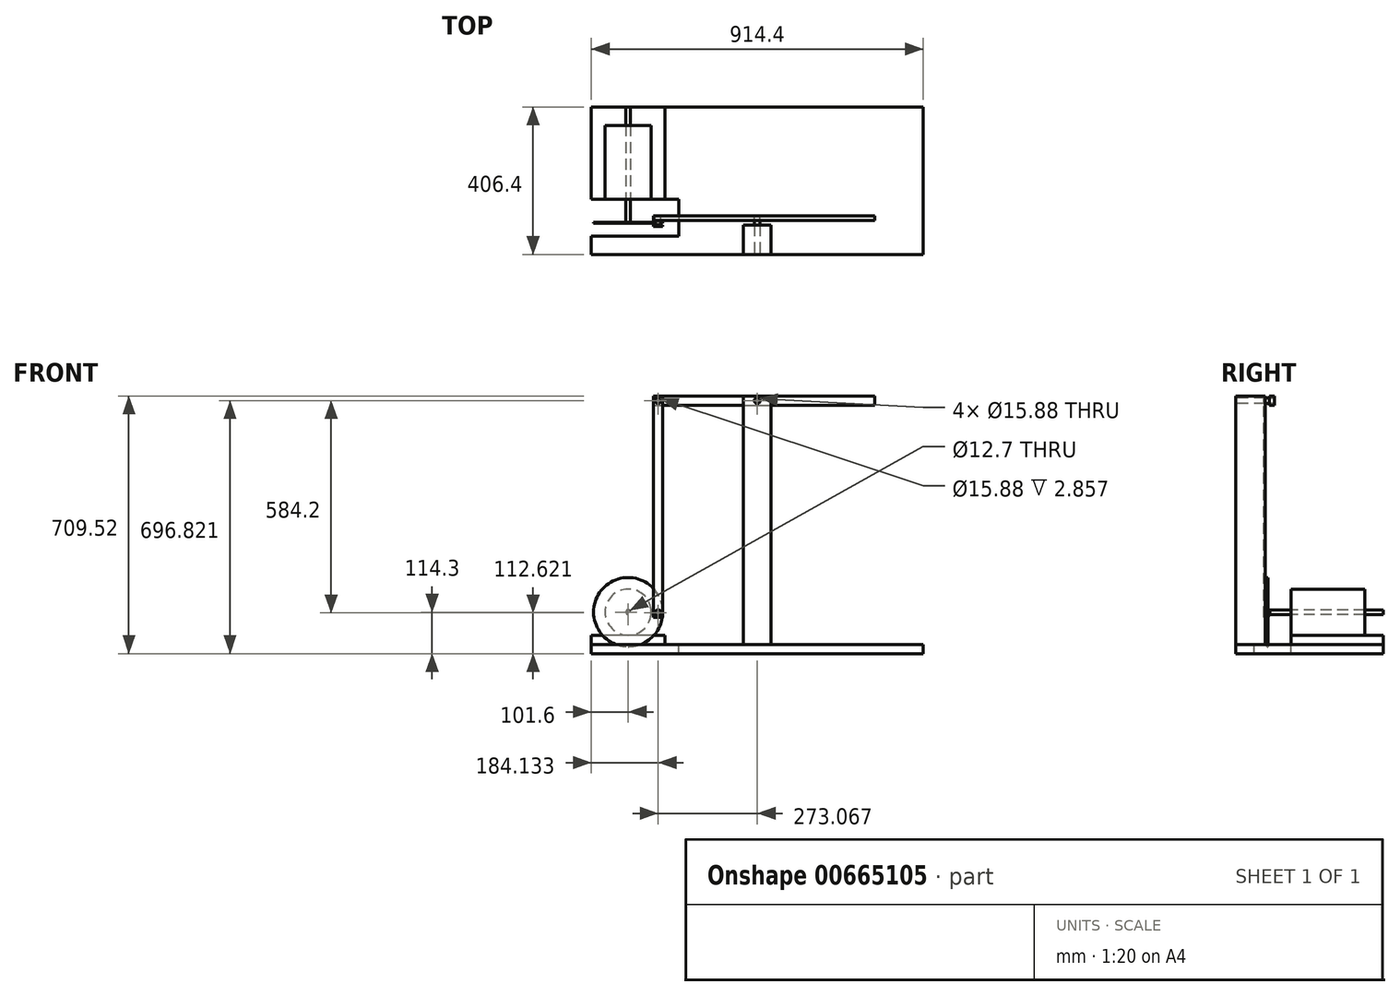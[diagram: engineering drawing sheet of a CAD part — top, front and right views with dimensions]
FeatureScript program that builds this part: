
annotation { "Feature Type Name" : "Feature", "Feature Type Description" : "" }
export const myFeature = defineFeature(function(context is Context, id is Id, definition is map)
    precondition{}
    {
        {
            var Q0;
            Q0=qCreatedBy(makeId("Top.planeOp"),FACE);
            var sketch = newSketch(context, id + "F0", { "sketchPlane" : qUnion([Q0])});
            skLineSegment(sketch, "E0.bottom", {"start": v(0, 0) * mm, "end": v(-203.2, 0) * mm});
            skLineSegment(sketch, "E0.top", {"start": v(0, -254) * mm, "end": v(-203.2, -254) * mm});
            skLineSegment(sketch, "E0.left", {"start": v(0, 0) * mm, "end": v(0, -254) * mm});
            skLineSegment(sketch, "E0.right", {"start": v(-203.2, 0) * mm, "end": v(-203.2, -254) * mm});
            skSolve(sketch);
        }
        {
            var Q0;
            Q0=makeQuery(id+"F0.imprint","IMPRINT",FACE,{"disambiguationData":[TD([[makeQuery(id+"F0.imprint","IMPRINT",EDGE,{"derivedFrom":sQuery(id+"F0.wireOp",EDGE,"E0.bottom")}),1.0]])]});
            extrude(context, id + "F1", {"entities" : qUnion([Q0]), "depth" : 25.4 * mm, "offsetDistance" : 25.4 * mm});
        }
        {
            var Q0;
            Q0=makeQuery(id+"F1.opExtrude","SWEPT_FACE",FACE,{"disambiguationData":[OSD([sQuery(id+"F0.wireOp",EDGE,"E0.top")])]});
            var sketch = newSketch(context, id + "F2", { "sketchPlane" : qUnion([Q0])});
            skLineSegment(sketch, "E1", {"start": v(-101.6, 25.4) * mm, "end": v(-101.6, 88.9) * mm, "construction": true});
            skCircle(sketch, "E2", {"center": v(-101.6, 88.9) * mm, "radius": 63.5 * mm});
            skCircle(sketch, "E3", {"center": v(-101.6, 88.9) * mm, "radius": 6.35 * mm});
            skSolve(sketch);
        }
        {
            var Q0;
            Q0 = qSketchRegion(id + "F2", true);
            extrude(context, id + "F3", {"entities" : qUnion([Q0]), "oppositeDirection" : true, "depth" : 203.2 * mm, "offsetDistance" : 25.4 * mm});
        }
        {
            var Q0;
            Q0=makeQuery(id+"F2.imprint","IMPRINT",FACE,{"disambiguationData":[TD([[makeQuery(id+"F2.imprint","IMPRINT",EDGE,{"derivedFrom":sQuery(id+"F2.wireOp",EDGE,"E3")}),1.0]])]});
            extrude(context, id + "F4", {"entities" : qUnion([Q0]), "depth" : 63.5 * mm, "offsetDistance" : 25.4 * mm, "hasSecondDirection" : true, "secondDirectionOppositeDirection" : true, "secondDirectionDepth" : 254 * mm});
        }
        {
            var Q0;
            Q0=makeQuery(id+"F4.opExtrude","CAP_FACE",FACE,{"disambiguationData":[OSD([sQuery(id+"F2.wireOp",EDGE,"E3")])],"isStart":false});
            var sketch = newSketch(context, id + "F5", { "sketchPlane" : qUnion([Q0])});
            skCircle(sketch, "E4.0", {"center": v(-101.6, 88.9) * mm, "radius": 6.35 * mm});
            skCircle(sketch, "E5", {"center": v(-101.6, 88.9) * mm, "radius": 95.25 * mm});
            skCircle(sketch, "E6", {"center": v(-101.6, 88.9) * mm, "radius": 82.55 * mm});
            skPoint(sketch, "E7", {"position": v(-19.07, 87.22) * mm});
            skCircle(sketch, "E8", {"center": v(-19.07, 87.22) * mm, "radius": 7.94 * mm});
            skSolve(sketch);
        }
        {
            var Q0;
            Q0=makeQuery(id+"F5.imprint","IMPRINT",FACE,{"disambiguationData":[TD([[makeQuery(id+"F5.imprint","IMPRINT",EDGE,{"derivedFrom":sQuery(id+"F5.wireOp",EDGE,"E5")}),1.0]])]});
            var Q1;
            Q1=makeQuery(id+"F5.imprint","IMPRINT",FACE,{"disambiguationData":[TD([[makeQuery(id+"F5.imprint","IMPRINT",EDGE,{"derivedFrom":sQuery(id+"F5.wireOp",EDGE,"E4.0")}),-1.0]])]});
            var Q2;
            Q2=makeQuery(id+"F5.imprint","IMPRINT",FACE,{"disambiguationData":[TD([[makeQuery(id+"F5.imprint","IMPRINT",EDGE,{"derivedFrom":sQuery(id+"F5.wireOp",EDGE,"E4.0")}),1.0]])]});
            extrude(context, id + "F6", {"entities" : qUnion([Q0, Q1, Q2]), "operationType" : NewBodyOperationType.ADD, "depth" : 3.17 * mm, "offsetDistance" : 25.4 * mm});
        }
        {
            var Q0;
            Q0=makeQuery(id+"F6.opExtrude","CAP_FACE",FACE,{"disambiguationData":[OSD([sQuery(id+"F5.wireOp",EDGE,"E5"),sQuery(id+"F5.wireOp",EDGE,"E8")])],"isStart":false});
            var sketch = newSketch(context, id + "F7", { "sketchPlane" : qUnion([Q0])});
            skCircle(sketch, "E9.0", {"center": v(-19.07, 87.22) * mm, "radius": 7.94 * mm});
            skSolve(sketch);
        }
        {
            var Q0;
            Q0=makeQuery(id+"F7.imprint","IMPRINT",FACE,{"disambiguationData":[TD([[makeQuery(id+"F7.imprint","IMPRINT",EDGE,{"derivedFrom":sQuery(id+"F7.wireOp",EDGE,"E9.0")}),1.0]])]});
            extrude(context, id + "F8", {"entities" : qUnion([Q0]), "operationType" : NewBodyOperationType.ADD, "endBound" : BoundingType.SYMMETRIC, "depth" : 15.88 * mm, "offsetDistance" : 25.4 * mm});
        }
        {
            var Q0;
            Q0=makeQuery(id+"F8.opExtrude","CAP_FACE",FACE,{"disambiguationData":[OSD([sQuery(id+"F7.wireOp",EDGE,"E9.0")])],"isStart":false});
            var sketch = newSketch(context, id + "F9", { "sketchPlane" : qUnion([Q0])});
            skLineSegment(sketch, "E10.bottom", {"start": v(-31.77, 74.52) * mm, "end": v(-6.37, 74.52) * mm});
            skLineSegment(sketch, "E10.top", {"start": v(-31.77, 684.12) * mm, "end": v(-6.37, 684.12) * mm});
            skLineSegment(sketch, "E10.left", {"start": v(-31.77, 74.52) * mm, "end": v(-31.77, 684.12) * mm});
            skLineSegment(sketch, "E10.right", {"start": v(-6.37, 74.52) * mm, "end": v(-6.37, 684.12) * mm});
            skLineSegment(sketch, "E11", {"start": v(-19.07, 74.52) * mm, "end": v(-19.07, 684.12) * mm, "construction": true});
            skPoint(sketch, "E12", {"position": v(-19.07, 87.22) * mm});
            skCircle(sketch, "E13.0", {"center": v(-19.07, 87.22) * mm, "radius": 7.94 * mm});
            skPoint(sketch, "E14", {"position": v(-19.07, 671.42) * mm});
            skCircle(sketch, "E15", {"center": v(-19.07, 671.42) * mm, "radius": 7.94 * mm});
            skSolve(sketch);
        }
        {
            var Q0;
            Q0=makeQuery(id+"F9.imprint","IMPRINT",FACE,{"disambiguationData":[TD([[makeQuery(id+"F9.imprint","IMPRINT",EDGE,{"derivedFrom":sQuery(id+"F9.wireOp",EDGE,"E10.bottom")}),1.0]])]});
            extrude(context, id + "F10", {"entities" : qUnion([Q0]), "oppositeDirection" : true, "depth" : 3.17 * mm, "offsetDistance" : 25.4 * mm});
        }
        {
            var Q0;
            Q0=makeQuery(id+"F0.imprint","IMPRINT",FACE,{"disambiguationData":[TD([[makeQuery(id+"F0.imprint","IMPRINT",EDGE,{"derivedFrom":sQuery(id+"F0.wireOp",EDGE,"E0.bottom")}),1.0]])]});
            var sketch = newSketch(context, id + "F11", { "sketchPlane" : qUnion([Q0])});
            skLineSegment(sketch, "E16.0.0", {"start": v(-203.2, -254) * mm, "end": v(0, -254) * mm});
            skLineSegment(sketch, "E16.0.1", {"start": v(0, -254) * mm, "end": v(0, 0) * mm});
            skLineSegment(sketch, "E16.0.2", {"start": v(0, 0) * mm, "end": v(-203.2, 0) * mm});
            skLineSegment(sketch, "E16.0.3", {"start": v(-203.2, 0) * mm, "end": v(-203.2, -254) * mm});
            skLineSegment(sketch, "E17.bottom", {"start": v(-203.2, 0) * mm, "end": v(711.2, 0) * mm});
            skLineSegment(sketch, "E17.top", {"start": v(-203.2, -406.4) * mm, "end": v(711.2, -406.4) * mm});
            skLineSegment(sketch, "E17.left", {"start": v(-203.2, 0) * mm, "end": v(-203.2, -406.4) * mm});
            skLineSegment(sketch, "E17.right", {"start": v(711.2, 0) * mm, "end": v(711.2, -406.4) * mm});
            skLineSegment(sketch, "E18", {"start": v(0, -254) * mm, "end": v(38.1, -254) * mm});
            skLineSegment(sketch, "E19", {"start": v(38.1, -254) * mm, "end": v(38.1, -355.6) * mm});
            skLineSegment(sketch, "E20", {"start": v(38.1, -355.6) * mm, "end": v(-203.2, -355.6) * mm});
            skSolve(sketch);
        }
        {
            var Q0;
            {var subQ0=sQuery(id+"F11.wireOp",EDGE,"E16.0.0");Q0=makeQuery(id+"F11.imprint","IMPRINT",FACE,{"disambiguationData":[TD([[makeQuery(id+"F11.imprint","IMPRINT",EDGE,{"derivedFrom":subQ0}),-1.0]])]});}
            var Q1;
            {var subQ4=sQuery(id+"F11.wireOp",EDGE,"E16.0.1");Q1=makeQuery(id+"F11.imprint","IMPRINT",FACE,{"disambiguationData":[TD([[makeQuery(id+"F11.imprint","IMPRINT",EDGE,{"derivedFrom":subQ4}),1.0]])]});}
            extrude(context, id + "F12", {"entities" : qUnion([Q0, Q1]), "oppositeDirection" : true, "depth" : 25.4 * mm, "offsetDistance" : 25.4 * mm});
        }
        {
            var Q0;
            Q0=makeQuery(id+"F12.opExtrude","SWEPT_FACE",FACE,{"disambiguationData":[OSD([sQuery(id+"F11.wireOp",EDGE,"E17.top")])]});
            var sketch = newSketch(context, id + "F13", { "sketchPlane" : qUnion([Q0])});
            skPoint(sketch, "E21.0", {"position": v(-6.37, 684.12) * mm});
            skLineSegment(sketch, "E22", {"start": v(254, 0) * mm, "end": v(254, 684.12) * mm, "construction": true});
            skLineSegment(sketch, "E23.bottom", {"start": v(254, 684.12) * mm, "end": v(292.1, 684.12) * mm});
            skLineSegment(sketch, "E23.top", {"start": v(254, 0) * mm, "end": v(292.1, 0) * mm});
            skLineSegment(sketch, "E23.left", {"start": v(254, 684.12) * mm, "end": v(254, 0) * mm});
            skLineSegment(sketch, "E23.right", {"start": v(292.1, 684.12) * mm, "end": v(292.1, 0) * mm});
            skLineSegment(sketch, "E24.MirrorCS", {"start": v(254, 684.12) * mm, "end": v(215.9, 684.12) * mm});
            skLineSegment(sketch, "E25.MirrorCS", {"start": v(215.9, 684.12) * mm, "end": v(215.9, 0) * mm});
            skLineSegment(sketch, "E26.0", {"start": v(-6.37, 74.52) * mm, "end": v(-6.37, 684.12) * mm});
            skSolve(sketch);
        }
        {
            var Q0;
            Q0=makeQuery(id+"F13.imprint","IMPRINT",FACE,{"disambiguationData":[TD([[makeQuery(id+"F13.imprint","IMPRINT",EDGE,{"derivedFrom":sQuery(id+"F13.wireOp",EDGE,"E23.bottom")}),-1.0]])]});
            var Q1;
            {var subQ0=sQuery(id+"F13.wireOp",EDGE,"E23.left");Q1=makeQuery(id+"F13.imprint","IMPRINT",FACE,{"disambiguationData":[TD([[makeQuery(id+"F13.imprint","IMPRINT",EDGE,{"derivedFrom":subQ0}),-1.0]])]});}
            extrude(context, id + "F14", {"entities" : qUnion([Q0, Q1]), "oppositeDirection" : true, "depth" : 80.64 * mm, "offsetDistance" : 25.4 * mm});
        }
        {
            var Q0;
            Q0=makeQuery(id+"F14.opExtrude","CAP_FACE",FACE,{"disambiguationData":[OSD([sQuery(id+"F11.wireOp",EDGE,"E17.top"),sQuery(id+"F13.wireOp",EDGE,"E23.bottom"),sQuery(id+"F13.wireOp",EDGE,"E23.top"),sQuery(id+"F13.wireOp",EDGE,"E23.right"),sQuery(id+"F13.wireOp",EDGE,"E24.MirrorCS"),sQuery(id+"F13.wireOp",EDGE,"E25.MirrorCS")])],"isStart":true});
            var sketch = newSketch(context, id + "F15", { "sketchPlane" : qUnion([Q0])});
            skLineSegment(sketch, "E27", {"start": v(254, 684.12) * mm, "end": v(254, 611) * mm, "construction": true});
            skLineSegment(sketch, "E28", {"start": v(215.9, 671.42) * mm, "end": v(292.1, 671.42) * mm, "construction": true});
            skCircle(sketch, "E29", {"center": v(254, 671.42) * mm, "radius": 7.94 * mm});
            skSolve(sketch);
        }
        {
            var Q0;
            Q0=makeQuery(id+"F15.imprint","IMPRINT",FACE,{"disambiguationData":[TD([[makeQuery(id+"F15.imprint","IMPRINT",EDGE,{"derivedFrom":sQuery(id+"F15.wireOp",EDGE,"E29")}),1.0]])]});
            extrude(context, id + "F16", {"entities" : qUnion([Q0]), "operationType" : NewBodyOperationType.REMOVE, "endBound" : BoundingType.UP_TO_NEXT, "oppositeDirection" : true, "depth" : 25.4 * mm, "offsetDistance" : 25.4 * mm});
        }
        {
            var Q0;
            Q0=makeQuery(id+"F14.opExtrude","CAP_FACE",FACE,{"disambiguationData":[OSD([sQuery(id+"F11.wireOp",EDGE,"E17.top"),sQuery(id+"F13.wireOp",EDGE,"E23.bottom"),sQuery(id+"F13.wireOp",EDGE,"E23.top"),sQuery(id+"F13.wireOp",EDGE,"E23.right"),sQuery(id+"F13.wireOp",EDGE,"E24.MirrorCS"),sQuery(id+"F13.wireOp",EDGE,"E25.MirrorCS")])],"isStart":false});
            var sketch = newSketch(context, id + "F17", { "sketchPlane" : qUnion([Q0])});
            skCircle(sketch, "E30.0", {"center": v(19.07, 671.42) * mm, "radius": 7.94 * mm});
            skCircle(sketch, "E31.0", {"center": v(-254, 671.42) * mm, "radius": 7.94 * mm});
            skSolve(sketch);
        }
        {
            var Q0;
            Q0=makeQuery(id+"F17.imprint","IMPRINT",FACE,{"disambiguationData":[TD([[makeQuery(id+"F17.imprint","IMPRINT",EDGE,{"derivedFrom":sQuery(id+"F17.wireOp",EDGE,"E31.0")}),1.0]])]});
            var Q1;
            Q1=makeQuery(id+"F17.imprint","IMPRINT",FACE,{"disambiguationData":[TD([[makeQuery(id+"F17.imprint","IMPRINT",EDGE,{"derivedFrom":sQuery(id+"F17.wireOp",EDGE,"E30.0")}),1.0]])]});
            extrude(context, id + "F18", {"entities" : qUnion([Q0, Q1]), "operationType" : NewBodyOperationType.ADD, "depth" : 25.4 * mm, "offsetDistance" : 25.4 * mm});
        }
        {
            var Q0;
            Q0=makeQuery(id+"F18.opExtrude","CAP_FACE",FACE,{"disambiguationData":[OSD([sQuery(id+"F17.wireOp",EDGE,"E30.0")])],"isStart":false});
            var sketch = newSketch(context, id + "F19", { "sketchPlane" : qUnion([Q0])});
            skLineSegment(sketch, "E32.bottom", {"start": v(31.77, 684.12) * mm, "end": v(-577.83, 684.12) * mm});
            skLineSegment(sketch, "E32.top", {"start": v(31.77, 658.72) * mm, "end": v(-577.83, 658.72) * mm});
            skLineSegment(sketch, "E32.left", {"start": v(31.77, 684.12) * mm, "end": v(31.77, 658.72) * mm});
            skLineSegment(sketch, "E32.right", {"start": v(-577.83, 684.12) * mm, "end": v(-577.83, 658.72) * mm});
            skLineSegment(sketch, "E33", {"start": v(-577.83, 671.42) * mm, "end": v(31.77, 671.42) * mm, "construction": true});
            skPoint(sketch, "E34", {"position": v(19.07, 671.42) * mm});
            skCircle(sketch, "E35.0.0", {"center": v(-254, 671.42) * mm, "radius": 7.94 * mm});
            skCircle(sketch, "E36.0", {"center": v(19.07, 671.42) * mm, "radius": 7.94 * mm});
            skSolve(sketch);
        }
        {
            var Q0;
            Q0=makeQuery(id+"F19.imprint","IMPRINT",FACE,{"disambiguationData":[TD([[makeQuery(id+"F19.imprint","IMPRINT",EDGE,{"derivedFrom":sQuery(id+"F19.wireOp",EDGE,"E32.bottom")}),1.0]])]});
            extrude(context, id + "F20", {"entities" : qUnion([Q0]), "oppositeDirection" : true, "depth" : 12.7 * mm, "offsetDistance" : 25.4 * mm});
        }
    });
